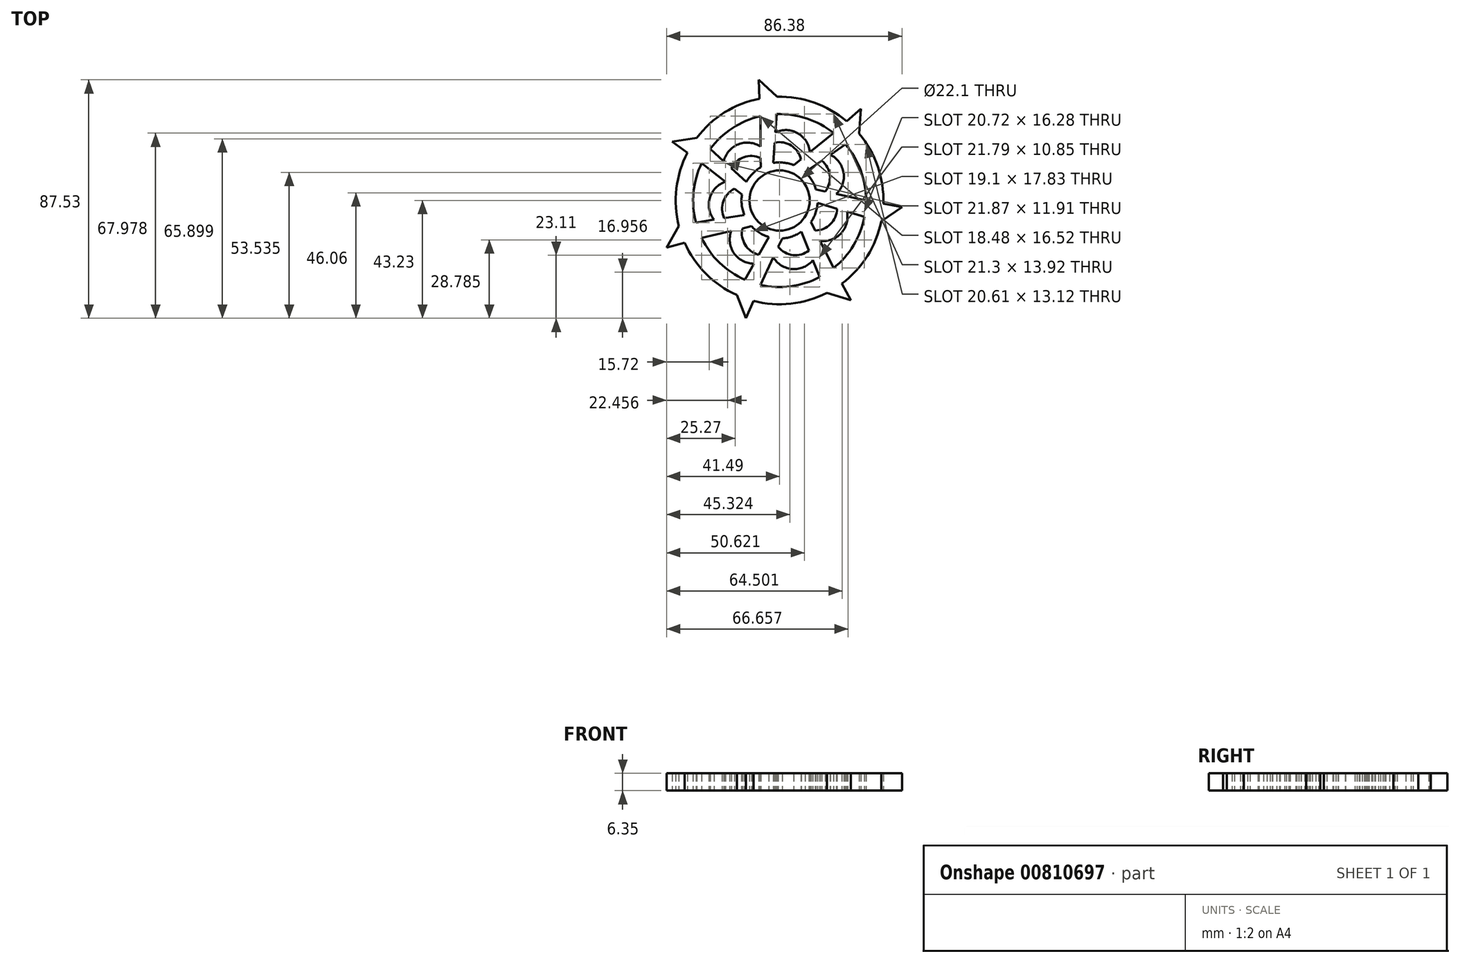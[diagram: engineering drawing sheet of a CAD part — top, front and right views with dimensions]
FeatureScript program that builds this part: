
annotation { "Feature Type Name" : "Feature", "Feature Type Description" : "" }
export const myFeature = defineFeature(function(context is Context, id is Id, definition is map)
    precondition{}
    {
        {
            var Q0;
            Q0=qCreatedBy(makeId("Top.planeOp"),FACE);
            var sketch = newSketch(context, id + "F0", { "sketchPlane" : qUnion([Q0])});
            skCircle(sketch, "E0", {"center": v(0, 0) * mm, "radius": 11.05 * mm});
            skCircle(sketch, "E1", {"center": v(0, 0) * mm, "radius": 31.73 * mm});
            skCircle(sketch, "E2", {"center": v(0, 0) * mm, "radius": 38.1 * mm});
            skLineSegment(sketch, "E3", {"start": v(0, 0) * mm, "end": v(-31.73, 0) * mm, "construction": true});
            skLineSegment(sketch, "E4", {"start": v(0, 0) * mm, "end": v(31.73, 0) * mm, "construction": true});
            skLineSegment(sketch, "E5", {"start": v(0, 0) * mm, "end": v(0, -31.73) * mm, "construction": true});
            skLineSegment(sketch, "E6.1.0", {"start": v(0, 0) * mm, "end": v(-31.75, 0) * mm, "construction": true});
            skLineSegment(sketch, "E6.2.0", {"start": v(0, 0) * mm, "end": v(0, -31.75) * mm, "construction": true});
            skLineSegment(sketch, "E6.3.0", {"start": v(0, 0) * mm, "end": v(31.75, 0) * mm, "construction": true});
            skLineSegment(sketch, "E7", {"start": v(0, 0) * mm, "end": v(0, 31.73) * mm, "construction": true});
            skLineSegment(sketch, "E8", {"start": v(9.95, 4.8) * mm, "end": v(31.73, 0) * mm});
            skLineSegment(sketch, "E9.1.0", {"start": v(2.45, 10.77) * mm, "end": v(19.78, 24.8) * mm});
            skLineSegment(sketch, "E9.2.0", {"start": v(-6.9, 8.63) * mm, "end": v(-7.06, 30.93) * mm});
            skLineSegment(sketch, "E9.3.0", {"start": v(-11.05, -0.01) * mm, "end": v(-28.58, 13.76) * mm});
            skLineSegment(sketch, "E9.4.0", {"start": v(-6.88, -8.65) * mm, "end": v(-28.58, -13.76) * mm});
            skLineSegment(sketch, "E9.5.0", {"start": v(2.47, -10.77) * mm, "end": v(-7.06, -30.93) * mm});
            skLineSegment(sketch, "E9.6.0", {"start": v(9.96, -4.78) * mm, "end": v(19.78, -24.8) * mm});
            skLineSegment(sketch, "E10", {"start": v(11.05, 0) * mm, "end": v(31.15, -6) * mm});
            skLineSegment(sketch, "E11.1.0", {"start": v(6.89, 8.64) * mm, "end": v(24.12, 20.61) * mm});
            skLineSegment(sketch, "E11.2.0", {"start": v(-2.46, 10.77) * mm, "end": v(-1.08, 31.7) * mm});
            skLineSegment(sketch, "E11.3.0", {"start": v(-9.95, 4.8) * mm, "end": v(-25.46, 18.93) * mm});
            skLineSegment(sketch, "E11.4.0", {"start": v(-9.95, -4.8) * mm, "end": v(-30.67, -8.1) * mm});
            skLineSegment(sketch, "E11.5.0", {"start": v(-2.46, -10.77) * mm, "end": v(-12.79, -29.03) * mm});
            skLineSegment(sketch, "E11.6.0", {"start": v(6.89, -8.64) * mm, "end": v(14.73, -28.1) * mm});
            skCircle(sketch, "E12", {"center": v(0, 0) * mm, "radius": 13.97 * mm});
            skLineSegment(sketch, "E13", {"start": v(31.75, 0) * mm, "end": v(38.08, -1.15) * mm, "construction": true});
            skLineSegment(sketch, "E14", {"start": v(31.15, -6) * mm, "end": v(37.34, -7.58) * mm, "construction": true});
            skLineSegment(sketch, "E15.1.0", {"start": v(19.8, 24.82) * mm, "end": v(24.64, 29.06) * mm, "construction": true});
            skLineSegment(sketch, "E15.1.1", {"start": v(24.12, 20.61) * mm, "end": v(29.2, 24.46) * mm, "construction": true});
            skLineSegment(sketch, "E15.2.0", {"start": v(-7.07, 30.95) * mm, "end": v(-7.35, 37.38) * mm, "construction": true});
            skLineSegment(sketch, "E15.2.1", {"start": v(-1.08, 31.7) * mm, "end": v(-0.92, 38.09) * mm, "construction": true});
            skLineSegment(sketch, "E15.3.0", {"start": v(-28.6, 13.78) * mm, "end": v(-33.81, 17.56) * mm, "construction": true});
            skLineSegment(sketch, "E15.3.1", {"start": v(-25.46, 18.93) * mm, "end": v(-30.35, 23.03) * mm, "construction": true});
            skLineSegment(sketch, "E15.4.0", {"start": v(-28.6, -13.78) * mm, "end": v(-34.81, -15.49) * mm, "construction": true});
            skLineSegment(sketch, "E15.4.1", {"start": v(-30.67, -8.1) * mm, "end": v(-36.93, -9.37) * mm, "construction": true});
            skLineSegment(sketch, "E15.5.0", {"start": v(-7.07, -30.95) * mm, "end": v(-9.6, -36.87) * mm, "construction": true});
            skLineSegment(sketch, "E15.5.1", {"start": v(-12.79, -29.03) * mm, "end": v(-15.7, -34.71) * mm, "construction": true});
            skLineSegment(sketch, "E15.6.0", {"start": v(19.8, -24.82) * mm, "end": v(22.85, -30.5) * mm, "construction": true});
            skLineSegment(sketch, "E15.6.1", {"start": v(14.73, -28.1) * mm, "end": v(17.35, -33.92) * mm, "construction": true});
            skLineSegment(sketch, "E16", {"start": v(38.08, -1.15) * mm, "end": v(44.89, -2.4) * mm});
            skLineSegment(sketch, "E17", {"start": v(44.89, -2.4) * mm, "end": v(37.34, -7.58) * mm});
            skLineSegment(sketch, "E18.1.0", {"start": v(29.87, 33.6) * mm, "end": v(29.2, 24.46) * mm});
            skLineSegment(sketch, "E18.1.1", {"start": v(24.64, 29.06) * mm, "end": v(29.87, 33.6) * mm});
            skLineSegment(sketch, "E18.2.0", {"start": v(-7.65, 44.3) * mm, "end": v(-0.92, 38.09) * mm});
            skLineSegment(sketch, "E18.2.1", {"start": v(-7.35, 37.38) * mm, "end": v(-7.65, 44.3) * mm});
            skLineSegment(sketch, "E18.3.0", {"start": v(-39.4, 21.64) * mm, "end": v(-30.35, 23.03) * mm});
            skLineSegment(sketch, "E18.3.1", {"start": v(-33.81, 17.56) * mm, "end": v(-39.4, 21.64) * mm});
            skLineSegment(sketch, "E18.4.0", {"start": v(-41.49, -17.31) * mm, "end": v(-36.93, -9.37) * mm});
            skLineSegment(sketch, "E18.4.1", {"start": v(-34.81, -15.49) * mm, "end": v(-41.49, -17.31) * mm});
            skLineSegment(sketch, "E18.5.0", {"start": v(-12.33, -43.23) * mm, "end": v(-15.7, -34.71) * mm});
            skLineSegment(sketch, "E18.5.1", {"start": v(-9.6, -36.87) * mm, "end": v(-12.33, -43.23) * mm});
            skLineSegment(sketch, "E18.6.0", {"start": v(26.1, -36.6) * mm, "end": v(17.35, -33.92) * mm});
            skLineSegment(sketch, "E18.6.1", {"start": v(22.85, -30.5) * mm, "end": v(26.1, -36.6) * mm});
            skArc(sketch, "E19", {"start": v(14.87, -14.8) * mm, "mid": v(22.59, -12) * mm, "end": v(24.72, -4.09) * mm});
            skArc(sketch, "E20", {"start": v(13.03, -11.03) * mm, "mid": v(18.7, -8.66) * mm, "end": v(21.1, -3) * mm});
            skArc(sketch, "E21.1.0", {"start": v(20.84, 2.4) * mm, "mid": v(23.47, 10.17) * mm, "end": v(18.6, 16.78) * mm});
            skArc(sketch, "E21.1.1", {"start": v(16.75, 3.3) * mm, "mid": v(18.42, 9.22) * mm, "end": v(15.5, 14.62) * mm});
            skArc(sketch, "E21.2.0", {"start": v(11.11, 17.79) * mm, "mid": v(6.68, 24.7) * mm, "end": v(-1.52, 25.01) * mm});
            skArc(sketch, "E21.2.1", {"start": v(7.86, 15.15) * mm, "mid": v(4.28, 20.15) * mm, "end": v(-1.77, 21.24) * mm});
            skArc(sketch, "E21.3.0", {"start": v(-6.98, 19.78) * mm, "mid": v(-15.14, 20.62) * mm, "end": v(-20.5, 14.4) * mm});
            skArc(sketch, "E21.3.1", {"start": v(-6.95, 15.6) * mm, "mid": v(-13.09, 15.91) * mm, "end": v(-17.7, 11.86) * mm});
            skArc(sketch, "E21.4.0", {"start": v(-19.82, 6.88) * mm, "mid": v(-25.56, 1.02) * mm, "end": v(-24.05, -7.05) * mm});
            skArc(sketch, "E21.4.1", {"start": v(-16.52, 4.29) * mm, "mid": v(-20.6, -0.31) * mm, "end": v(-20.31, -6.45) * mm});
            skArc(sketch, "E21.5.0", {"start": v(-17.73, -11.2) * mm, "mid": v(-16.73, -19.35) * mm, "end": v(-9.49, -23.2) * mm});
            skArc(sketch, "E21.5.1", {"start": v(-13.66, -10.24) * mm, "mid": v(-12.6, -16.3) * mm, "end": v(-7.62, -19.9) * mm});
            skArc(sketch, "E21.6.0", {"start": v(-2.3, -20.85) * mm, "mid": v(4.7, -25.15) * mm, "end": v(12.22, -21.88) * mm});
            skArc(sketch, "E21.6.1", {"start": v(-0.5, -17.06) * mm, "mid": v(4.89, -20.01) * mm, "end": v(10.8, -18.37) * mm});
            skSolve(sketch);
        }
        {
            var Q0;
            Q0=makeQuery(id+"F0.imprint","IMPRINT",FACE,{"disambiguationData":[TD([[makeQuery(id+"F0.imprint","IMPRINT",EDGE,{"derivedFrom":sQuery(id+"F0.wireOp",EDGE,"E2")}),1.0]])]});
            var Q1;
            {var subQ0=sQuery(id+"F0.wireOp",EDGE,"E9.4.0");Q1=makeQuery(id+"F0.imprint","IMPRINT",FACE,{"disambiguationData":[TD([[makeQuery(id+"F0.imprint","IMPRINT",EDGE,{"derivedFrom":subQ0}),-1.0]])]});}
            var Q2;
            {var subQ0=sQuery(id+"F0.wireOp",EDGE,"E9.3.0");Q2=makeQuery(id+"F0.imprint","IMPRINT",FACE,{"disambiguationData":[TD([[makeQuery(id+"F0.imprint","IMPRINT",EDGE,{"derivedFrom":subQ0}),-1.0]])]});}
            var Q3;
            {var subQ0=sQuery(id+"F0.wireOp",EDGE,"E9.2.0");Q3=makeQuery(id+"F0.imprint","IMPRINT",FACE,{"disambiguationData":[TD([[makeQuery(id+"F0.imprint","IMPRINT",EDGE,{"derivedFrom":subQ0}),-1.0]])]});}
            var Q4;
            {var subQ0=sQuery(id+"F0.wireOp",EDGE,"E9.1.0");Q4=makeQuery(id+"F0.imprint","IMPRINT",FACE,{"disambiguationData":[TD([[makeQuery(id+"F0.imprint","IMPRINT",EDGE,{"derivedFrom":subQ0}),-1.0]])]});}
            var Q5;
            {var subQ0=sQuery(id+"F0.wireOp",EDGE,"E8");Q5=makeQuery(id+"F0.imprint","IMPRINT",FACE,{"disambiguationData":[TD([[makeQuery(id+"F0.imprint","IMPRINT",EDGE,{"derivedFrom":subQ0}),-1.0]])]});}
            var Q6;
            {var subQ0=sQuery(id+"F0.wireOp",EDGE,"E9.6.0");Q6=makeQuery(id+"F0.imprint","IMPRINT",FACE,{"disambiguationData":[TD([[makeQuery(id+"F0.imprint","IMPRINT",EDGE,{"derivedFrom":subQ0}),-1.0]])]});}
            var Q7;
            {var subQ0=sQuery(id+"F0.wireOp",EDGE,"E9.5.0");Q7=makeQuery(id+"F0.imprint","IMPRINT",FACE,{"disambiguationData":[TD([[makeQuery(id+"F0.imprint","IMPRINT",EDGE,{"derivedFrom":subQ0}),-1.0]])]});}
            var Q8;
            {var subQ0=sQuery(id+"F0.wireOp",EDGE,"E9.2.0");var subQ1=sQuery(id+"F0.wireOp",EDGE,"E0");var subQ2=makeQuery(id+"F0.imprint","INTERSECT",VERTEX,{"derivedFrom":[subQ1,subQ0]});Q8=makeQuery(id+"F0.imprint","IMPRINT",FACE,{"disambiguationData":[TD([[makeQuery(id+"F0.imprint","IMPRINT",EDGE,{"disambiguationData":[TD([[subQ2,-1.0]])],"derivedFrom":subQ1}),-1.0]])]});}
            var Q9;
            {var subQ0=sQuery(id+"F0.wireOp",EDGE,"E9.3.0");var subQ1=sQuery(id+"F0.wireOp",EDGE,"E0");var subQ2=makeQuery(id+"F0.imprint","INTERSECT",VERTEX,{"derivedFrom":[subQ1,subQ0]});Q9=makeQuery(id+"F0.imprint","IMPRINT",FACE,{"disambiguationData":[TD([[makeQuery(id+"F0.imprint","IMPRINT",EDGE,{"disambiguationData":[TD([[subQ2,-1.0]])],"derivedFrom":subQ1}),-1.0]])]});}
            var Q10;
            {var subQ0=sQuery(id+"F0.wireOp",EDGE,"E9.4.0");var subQ1=sQuery(id+"F0.wireOp",EDGE,"E0");var subQ2=makeQuery(id+"F0.imprint","INTERSECT",VERTEX,{"derivedFrom":[subQ1,subQ0]});Q10=makeQuery(id+"F0.imprint","IMPRINT",FACE,{"disambiguationData":[TD([[makeQuery(id+"F0.imprint","IMPRINT",EDGE,{"disambiguationData":[TD([[subQ2,-1.0]])],"derivedFrom":subQ1}),-1.0]])]});}
            var Q11;
            {var subQ0=sQuery(id+"F0.wireOp",EDGE,"E9.5.0");var subQ1=sQuery(id+"F0.wireOp",EDGE,"E0");var subQ2=makeQuery(id+"F0.imprint","INTERSECT",VERTEX,{"derivedFrom":[subQ1,subQ0]});Q11=makeQuery(id+"F0.imprint","IMPRINT",FACE,{"disambiguationData":[TD([[makeQuery(id+"F0.imprint","IMPRINT",EDGE,{"disambiguationData":[TD([[subQ2,-1.0]])],"derivedFrom":subQ1}),-1.0]])]});}
            var Q12;
            {var subQ0=sQuery(id+"F0.wireOp",EDGE,"E9.6.0");var subQ1=sQuery(id+"F0.wireOp",EDGE,"E0");var subQ2=makeQuery(id+"F0.imprint","INTERSECT",VERTEX,{"derivedFrom":[subQ1,subQ0]});Q12=makeQuery(id+"F0.imprint","IMPRINT",FACE,{"disambiguationData":[TD([[makeQuery(id+"F0.imprint","IMPRINT",EDGE,{"disambiguationData":[TD([[subQ2,-1.0]])],"derivedFrom":subQ1}),-1.0]])]});}
            var Q13;
            {var subQ0=sQuery(id+"F0.wireOp",EDGE,"E8");var subQ1=sQuery(id+"F0.wireOp",EDGE,"E0");var subQ2=makeQuery(id+"F0.imprint","INTERSECT",VERTEX,{"derivedFrom":[subQ1,subQ0]});Q13=makeQuery(id+"F0.imprint","IMPRINT",FACE,{"disambiguationData":[TD([[makeQuery(id+"F0.imprint","IMPRINT",EDGE,{"disambiguationData":[TD([[subQ2,-1.0]])],"derivedFrom":subQ1}),-1.0]])]});}
            var Q14;
            {var subQ0=sQuery(id+"F0.wireOp",EDGE,"E9.1.0");var subQ1=sQuery(id+"F0.wireOp",EDGE,"E0");var subQ2=makeQuery(id+"F0.imprint","INTERSECT",VERTEX,{"derivedFrom":[subQ1,subQ0]});Q14=makeQuery(id+"F0.imprint","IMPRINT",FACE,{"disambiguationData":[TD([[makeQuery(id+"F0.imprint","IMPRINT",EDGE,{"disambiguationData":[TD([[subQ2,-1.0]])],"derivedFrom":subQ1}),-1.0]])]});}
            var Q15;
            {var subQ0=sQuery(id+"F0.wireOp",EDGE,"E18.4.0");Q15=makeQuery(id+"F0.imprint","IMPRINT",FACE,{"disambiguationData":[TD([[makeQuery(id+"F0.imprint","IMPRINT",EDGE,{"derivedFrom":subQ0}),-1.0]])]});}
            var Q16;
            {var subQ0=sQuery(id+"F0.wireOp",EDGE,"E18.3.0");Q16=makeQuery(id+"F0.imprint","IMPRINT",FACE,{"disambiguationData":[TD([[makeQuery(id+"F0.imprint","IMPRINT",EDGE,{"derivedFrom":subQ0}),-1.0]])]});}
            var Q17;
            {var subQ0=sQuery(id+"F0.wireOp",EDGE,"E18.2.0");Q17=makeQuery(id+"F0.imprint","IMPRINT",FACE,{"disambiguationData":[TD([[makeQuery(id+"F0.imprint","IMPRINT",EDGE,{"derivedFrom":subQ0}),-1.0]])]});}
            var Q18;
            {var subQ0=sQuery(id+"F0.wireOp",EDGE,"E18.1.0");Q18=makeQuery(id+"F0.imprint","IMPRINT",FACE,{"disambiguationData":[TD([[makeQuery(id+"F0.imprint","IMPRINT",EDGE,{"derivedFrom":subQ0}),-1.0]])]});}
            var Q19;
            {var subQ0=sQuery(id+"F0.wireOp",EDGE,"E16");Q19=makeQuery(id+"F0.imprint","IMPRINT",FACE,{"disambiguationData":[TD([[makeQuery(id+"F0.imprint","IMPRINT",EDGE,{"derivedFrom":subQ0}),-1.0]])]});}
            var Q20;
            {var subQ0=sQuery(id+"F0.wireOp",EDGE,"E18.6.0");Q20=makeQuery(id+"F0.imprint","IMPRINT",FACE,{"disambiguationData":[TD([[makeQuery(id+"F0.imprint","IMPRINT",EDGE,{"derivedFrom":subQ0}),-1.0]])]});}
            var Q21;
            {var subQ0=sQuery(id+"F0.wireOp",EDGE,"E18.5.0");Q21=makeQuery(id+"F0.imprint","IMPRINT",FACE,{"disambiguationData":[TD([[makeQuery(id+"F0.imprint","IMPRINT",EDGE,{"derivedFrom":subQ0}),-1.0]])]});}
            var Q22;
            {var subQ0=sQuery(id+"F0.wireOp",EDGE,"E21.3.0");Q22=makeQuery(id+"F0.imprint","IMPRINT",FACE,{"disambiguationData":[TD([[makeQuery(id+"F0.imprint","IMPRINT",EDGE,{"derivedFrom":subQ0}),1.0]])]});}
            var Q23;
            {var subQ0=sQuery(id+"F0.wireOp",EDGE,"E21.2.0");Q23=makeQuery(id+"F0.imprint","IMPRINT",FACE,{"disambiguationData":[TD([[makeQuery(id+"F0.imprint","IMPRINT",EDGE,{"derivedFrom":subQ0}),1.0]])]});}
            var Q24;
            {var subQ0=sQuery(id+"F0.wireOp",EDGE,"E21.1.0");Q24=makeQuery(id+"F0.imprint","IMPRINT",FACE,{"disambiguationData":[TD([[makeQuery(id+"F0.imprint","IMPRINT",EDGE,{"derivedFrom":subQ0}),1.0]])]});}
            var Q25;
            {var subQ0=sQuery(id+"F0.wireOp",EDGE,"E19");Q25=makeQuery(id+"F0.imprint","IMPRINT",FACE,{"disambiguationData":[TD([[makeQuery(id+"F0.imprint","IMPRINT",EDGE,{"derivedFrom":subQ0}),1.0]])]});}
            var Q26;
            {var subQ0=sQuery(id+"F0.wireOp",EDGE,"E21.4.0");Q26=makeQuery(id+"F0.imprint","IMPRINT",FACE,{"disambiguationData":[TD([[makeQuery(id+"F0.imprint","IMPRINT",EDGE,{"derivedFrom":subQ0}),1.0]])]});}
            var Q27;
            {var subQ0=sQuery(id+"F0.wireOp",EDGE,"E21.6.0");Q27=makeQuery(id+"F0.imprint","IMPRINT",FACE,{"disambiguationData":[TD([[makeQuery(id+"F0.imprint","IMPRINT",EDGE,{"derivedFrom":subQ0}),1.0]])]});}
            var Q28;
            {var subQ0=sQuery(id+"F0.wireOp",EDGE,"E21.5.0");Q28=makeQuery(id+"F0.imprint","IMPRINT",FACE,{"disambiguationData":[TD([[makeQuery(id+"F0.imprint","IMPRINT",EDGE,{"derivedFrom":subQ0}),1.0]])]});}
            var Q29;
            {var subQ0=sQuery(id+"F0.wireOp",EDGE,"E9.3.0");var subQ1=sQuery(id+"F0.wireOp",EDGE,"E0");var subQ2=makeQuery(id+"F0.imprint","INTERSECT",VERTEX,{"derivedFrom":[subQ1,subQ0]});Q29=makeQuery(id+"F0.imprint","IMPRINT",FACE,{"disambiguationData":[TD([[makeQuery(id+"F0.imprint","IMPRINT",EDGE,{"disambiguationData":[TD([[subQ2,1.0]])],"derivedFrom":subQ1}),-1.0]])]});}
            var Q30;
            {var subQ0=sQuery(id+"F0.wireOp",EDGE,"E9.4.0");var subQ1=sQuery(id+"F0.wireOp",EDGE,"E0");var subQ2=makeQuery(id+"F0.imprint","INTERSECT",VERTEX,{"derivedFrom":[subQ1,subQ0]});Q30=makeQuery(id+"F0.imprint","IMPRINT",FACE,{"disambiguationData":[TD([[makeQuery(id+"F0.imprint","IMPRINT",EDGE,{"disambiguationData":[TD([[subQ2,1.0]])],"derivedFrom":subQ1}),-1.0]])]});}
            var Q31;
            {var subQ0=sQuery(id+"F0.wireOp",EDGE,"E9.5.0");var subQ1=sQuery(id+"F0.wireOp",EDGE,"E0");var subQ2=makeQuery(id+"F0.imprint","INTERSECT",VERTEX,{"derivedFrom":[subQ1,subQ0]});Q31=makeQuery(id+"F0.imprint","IMPRINT",FACE,{"disambiguationData":[TD([[makeQuery(id+"F0.imprint","IMPRINT",EDGE,{"disambiguationData":[TD([[subQ2,1.0]])],"derivedFrom":subQ1}),-1.0]])]});}
            var Q32;
            {var subQ0=sQuery(id+"F0.wireOp",EDGE,"E9.6.0");var subQ1=sQuery(id+"F0.wireOp",EDGE,"E0");var subQ2=makeQuery(id+"F0.imprint","INTERSECT",VERTEX,{"derivedFrom":[subQ1,subQ0]});Q32=makeQuery(id+"F0.imprint","IMPRINT",FACE,{"disambiguationData":[TD([[makeQuery(id+"F0.imprint","IMPRINT",EDGE,{"disambiguationData":[TD([[subQ2,1.0]])],"derivedFrom":subQ1}),-1.0]])]});}
            var Q33;
            {var subQ0=sQuery(id+"F0.wireOp",EDGE,"E8");var subQ1=sQuery(id+"F0.wireOp",EDGE,"E0");var subQ2=makeQuery(id+"F0.imprint","INTERSECT",VERTEX,{"derivedFrom":[subQ1,subQ0]});Q33=makeQuery(id+"F0.imprint","IMPRINT",FACE,{"disambiguationData":[TD([[makeQuery(id+"F0.imprint","IMPRINT",EDGE,{"disambiguationData":[TD([[subQ2,1.0]])],"derivedFrom":subQ1}),-1.0]])]});}
            var Q34;
            {var subQ0=sQuery(id+"F0.wireOp",EDGE,"E9.1.0");var subQ1=sQuery(id+"F0.wireOp",EDGE,"E0");var subQ2=makeQuery(id+"F0.imprint","INTERSECT",VERTEX,{"derivedFrom":[subQ1,subQ0]});Q34=makeQuery(id+"F0.imprint","IMPRINT",FACE,{"disambiguationData":[TD([[makeQuery(id+"F0.imprint","IMPRINT",EDGE,{"disambiguationData":[TD([[subQ2,1.0]])],"derivedFrom":subQ1}),-1.0]])]});}
            var Q35;
            {var subQ0=sQuery(id+"F0.wireOp",EDGE,"E9.2.0");var subQ1=sQuery(id+"F0.wireOp",EDGE,"E0");var subQ2=makeQuery(id+"F0.imprint","INTERSECT",VERTEX,{"derivedFrom":[subQ1,subQ0]});Q35=makeQuery(id+"F0.imprint","IMPRINT",FACE,{"disambiguationData":[TD([[makeQuery(id+"F0.imprint","IMPRINT",EDGE,{"disambiguationData":[TD([[subQ2,1.0]])],"derivedFrom":subQ1}),-1.0]])]});}
            extrude(context, id + "F1", {"entities" : qUnion([Q0, Q1, Q2, Q3, Q4, Q5, Q6, Q7, Q8, Q9, Q10, Q11, Q12, Q13, Q14, Q15, Q16, Q17, Q18, Q19, Q20, Q21, Q22, Q23, Q24, Q25, Q26, Q27, Q28, Q29, Q30, Q31, Q32, Q33, Q34, Q35]), "depth" : 6.35 * mm, "offsetDistance" : 25.4 * mm});
        }
    });
